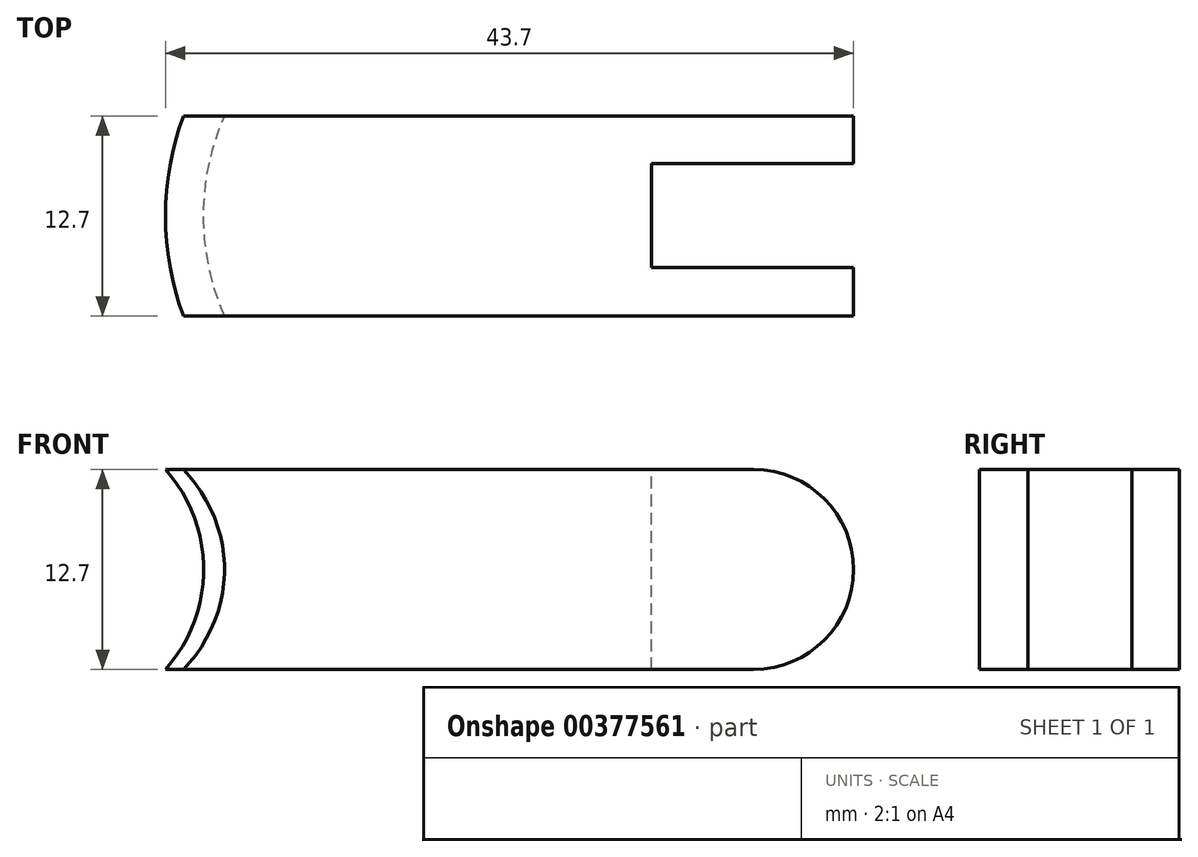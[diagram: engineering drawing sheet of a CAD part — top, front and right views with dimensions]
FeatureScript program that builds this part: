
annotation { "Feature Type Name" : "Feature", "Feature Type Description" : "" }
export const myFeature = defineFeature(function(context is Context, id is Id, definition is map)
    precondition{}
    {
        {
            var Q0;
            Q0=qCreatedBy(makeId("Top.planeOp"),FACE);
            var sketch = newSketch(context, id + "F0", { "sketchPlane" : qUnion([Q0])});
            skLineSegment(sketch, "E0.bottom", {"start": v(0, 12.7) * mm, "end": v(50.8, 12.7) * mm});
            skLineSegment(sketch, "E0.top", {"start": v(0, 0) * mm, "end": v(50.8, 0) * mm});
            skLineSegment(sketch, "E0.left", {"start": v(0, 12.7) * mm, "end": v(0, 0) * mm});
            skLineSegment(sketch, "E0.right", {"start": v(50.8, 12.7) * mm, "end": v(50.8, 0) * mm});
            skSolve(sketch);
        }
        {
            var Q0;
            Q0 = qSketchRegion(id + "F0", true);
            extrude(context, id + "F1", {"entities" : qUnion([Q0]), "depth" : 12.7 * mm});
        }
        {
            var Q0;
            Q0=makeQuery(id+"F1.opExtrude","CAP_EDGE",EDGE,{"disambiguationData":[OSD([sQuery(id+"F0.wireOp",EDGE,"E0.right")])],"isStart":false});
            cPoint(context, id + "F2", {"entities" : qUnion([Q0]), "parameter" : 0.5});
        }
        {
            var Q0;
            Q0=makeQuery(id+"F1.opExtrude","CAP_EDGE",EDGE,{"disambiguationData":[OSD([sQuery(id+"F0.wireOp",EDGE,"E0.left")])],"isStart":false});
            cPoint(context, id + "F3", {"entities" : qUnion([Q0]), "parameter" : 0.5});
        }
        {
            var Q0;
            Q0=makeQuery(id+"F1.opExtrude","CAP_EDGE",EDGE,{"disambiguationData":[OSD([sQuery(id+"F0.wireOp",EDGE,"E0.left")])],"isStart":true});
            cPoint(context, id + "F4", {"entities" : qUnion([Q0]), "parameter" : 0.5});
        }
        {
            var Q0;
            Q0 = qCreatedBy(id + "F2" ,VERTEX);
            var Q1;
            Q1 = qCreatedBy(id + "F3" ,VERTEX);
            var Q2;
            Q2 = qCreatedBy(id + "F4" ,VERTEX);
            cPlane(context, id + "F5", {"entities" : qUnion([Q0, Q1, Q2]), "cplaneType" : CPlaneType.THREE_POINT, "offset" : 25.4 * mm, "width" : 152.4 * mm, "height" : 152.4 * mm});
        }
        {
            var Q0;
            Q0=qCreatedBy(id+"F5.planeOp",FACE);
            var sketch = newSketch(context, id + "F6", { "sketchPlane" : qUnion([Q0])});
            skCircle(sketch, "E1", {"center": v(0, 6.35) * mm, "radius": 9.53 * mm});
            skLineSegment(sketch, "E2", {"start": v(-25.4, 12.66) * mm, "end": v(-25.4, 0) * mm});
            skSolve(sketch);
        }
        {
            var Q0;
            Q0=makeQuery(id+"F6.imprint","IMPRINT",FACE,{"disambiguationData":[TD([[makeQuery(id+"F6.imprint","IMPRINT",EDGE,{"derivedFrom":sQuery(id+"F6.wireOp",EDGE,"E1")}),1.0]])]});
            var Q1;
            Q1=sQuery(id+"F6.wireOp",EDGE,"E2");
            revolve(context, id + "F7", {"operationType" : NewBodyOperationType.REMOVE, "entities" : qUnion([Q0]), "axis" : qUnion([Q1]), "revolveType" : RevolveType.TWO_DIRECTIONS, "oppositeDirection" : true, "angle" : 30 * degree, "angleBack" : 330 * degree});
        }
        {
            var Q0;
            Q0=makeQuery(id+"F1.opExtrude","SWEPT_FACE",FACE,{"disambiguationData":[OSD([sQuery(id+"F0.wireOp",EDGE,"E0.bottom")])]});
            var sketch = newSketch(context, id + "F8", { "sketchPlane" : qUnion([Q0])});
            skArc(sketch, "E3", {"start": v(-44.45, 12.7) * mm, "mid": v(-50.8, 6.35) * mm, "end": v(-44.45, 0) * mm});
            skLineSegment(sketch, "E4", {"start": v(-44.45, 12.7) * mm, "end": v(-50.8, 12.7) * mm});
            skLineSegment(sketch, "E5", {"start": v(-50.8, 12.7) * mm, "end": v(-50.8, 0) * mm});
            skLineSegment(sketch, "E6", {"start": v(-50.8, 0) * mm, "end": v(-44.45, 0) * mm});
            skSolve(sketch);
        }
        {
            var Q0;
            {var subQ0=sQuery(id+"F8.wireOp",EDGE,"E4");Q0=makeQuery(id+"F8.imprint","IMPRINT",FACE,{"disambiguationData":[TD([[makeQuery(id+"F8.imprint","IMPRINT",EDGE,{"derivedFrom":subQ0}),1.0]])]});}
            var Q1;
            {var subQ0=sQuery(id+"F8.wireOp",EDGE,"E6");Q1=makeQuery(id+"F8.imprint","IMPRINT",FACE,{"disambiguationData":[TD([[makeQuery(id+"F8.imprint","IMPRINT",EDGE,{"derivedFrom":subQ0}),-1.0]])]});}
            extrude(context, id + "F9", {"entities" : qUnion([Q0, Q1]), "operationType" : NewBodyOperationType.REMOVE, "oppositeDirection" : true, "depth" : 25.4 * mm});
        }
        {
            var Q0;
            Q0=makeQuery(id+"F1.opExtrude","CAP_FACE",FACE,{"disambiguationData":[OSD([sQuery(id+"F0.wireOp",EDGE,"E0.bottom"),sQuery(id+"F0.wireOp",EDGE,"E0.top"),sQuery(id+"F0.wireOp",EDGE,"E0.left"),sQuery(id+"F0.wireOp",EDGE,"E0.right")])],"isStart":false});
            var sketch = newSketch(context, id + "F10", { "sketchPlane" : qUnion([Q0])});
            skLineSegment(sketch, "E7.bottom", {"start": v(50.8, 6.39) * mm, "end": v(37.97, 6.39) * mm});
            skLineSegment(sketch, "E7.top", {"start": v(50.8, 9.69) * mm, "end": v(37.97, 9.69) * mm});
            skLineSegment(sketch, "E7.left", {"start": v(50.8, 6.39) * mm, "end": v(50.8, 9.69) * mm});
            skLineSegment(sketch, "E7.right", {"start": v(37.97, 6.39) * mm, "end": v(37.97, 9.69) * mm});
            skLineSegment(sketch, "E8.MirrorCS", {"start": v(37.97, 6.39) * mm, "end": v(37.97, 3.08) * mm});
            skLineSegment(sketch, "E9.MirrorCS", {"start": v(50.8, 3.08) * mm, "end": v(37.97, 3.08) * mm});
            skLineSegment(sketch, "E10.MirrorCS", {"start": v(50.8, 6.39) * mm, "end": v(50.8, 3.08) * mm});
            skSolve(sketch);
        }
        {
            var Q0;
            Q0 = qSketchRegion(id + "F10", true);
            extrude(context, id + "F11", {"entities" : qUnion([Q0]), "operationType" : NewBodyOperationType.REMOVE, "oppositeDirection" : true, "depth" : 25.4 * mm});
        }
    });
